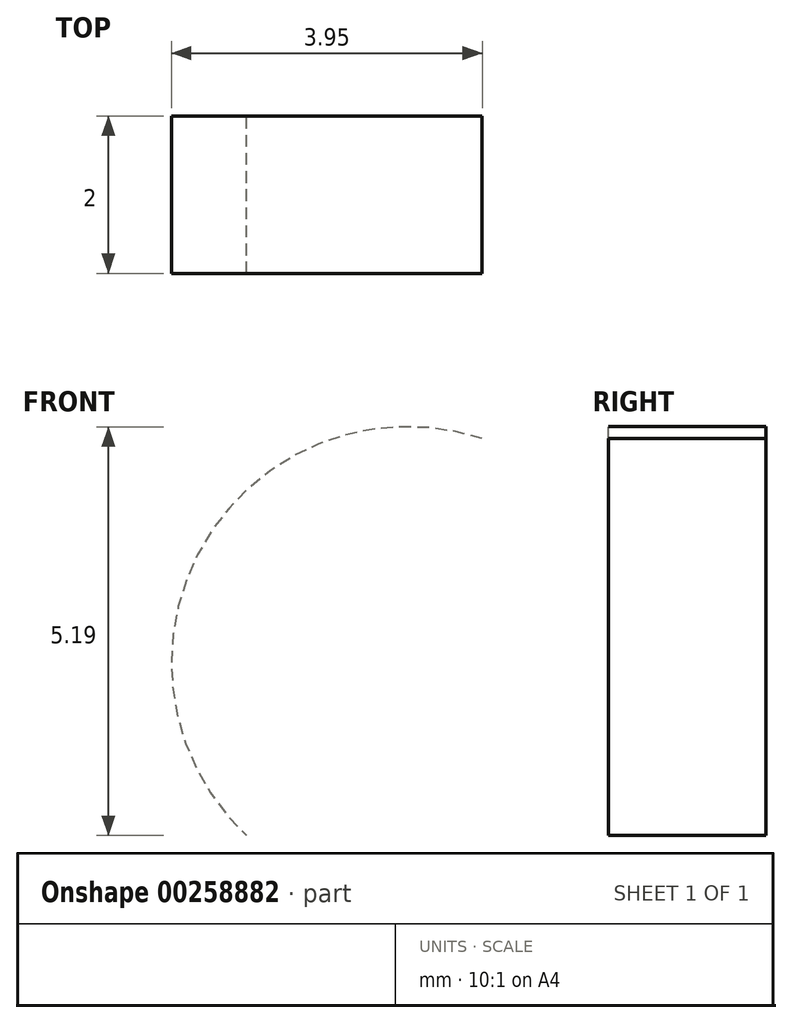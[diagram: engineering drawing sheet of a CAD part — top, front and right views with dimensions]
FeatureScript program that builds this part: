
annotation { "Feature Type Name" : "Feature", "Feature Type Description" : "" }
export const myFeature = defineFeature(function(context is Context, id is Id, definition is map)
    precondition{}
    {
        {
            var Q0;
            Q0=qCreatedBy(makeId("Front.planeOp"),FACE);
            var sketch = newSketch(context, id + "F0", { "sketchPlane" : qUnion([Q0])});
            skCircle(sketch, "E0", {"center": v(15, 2.03) * mm, "radius": 1.75 * mm});
            skCircle(sketch, "E1", {"center": v(0, -2.97) * mm, "radius": 1.75 * mm});
            skArc(sketch, "E2", {"start": v(17.04, -0.17) * mm, "mid": v(17.58, 3.56) * mm, "end": v(14.05, 4.88) * mm});
            skLineSegment(sketch, "E3", {"start": v(14.05, 4.88) * mm, "end": v(1.58, 0.72) * mm});
            skCircle(sketch, "E4.MirrorC", {"center": v(-15, 2.03) * mm, "radius": 1.75 * mm});
            skArc(sketch, "E5.MirrorC", {"start": v(-17.03, -0.17) * mm, "mid": v(-17.58, 3.56) * mm, "end": v(-14.05, 4.88) * mm});
            skLineSegment(sketch, "E6.MirrorCS", {"start": v(-14.05, 4.88) * mm, "end": v(-1.58, 0.72) * mm});
            skArc(sketch, "E7.filletArc", {"start": v(-1.58, 0.72) * mm, "mid": v(0, 0.47) * mm, "end": v(1.58, 0.72) * mm});
            skCircle(sketch, "E8", {"center": v(0, -9.47) * mm, "radius": 3.5 * mm});
            skArc(sketch, "E9", {"start": v(-3.23, -12.95) * mm, "mid": v(0, -14.22) * mm, "end": v(3.23, -12.95) * mm});
            skLineSegment(sketch, "E10", {"start": v(3.23, -12.95) * mm, "end": v(17.22, 0) * mm});
            skLineSegment(sketch, "E11.MirrorCS", {"start": v(-3.23, -12.95) * mm, "end": v(-17.22, 0) * mm});
            skSolve(sketch);
        }
        {
            var Q0;
            {var subQ0=sQuery(id+"F0.wireOp",EDGE,"E5.MirrorC");Q0=makeQuery(id+"F0.imprint","IMPRINT",FACE,{"disambiguationData":[TD([[makeQuery(id+"F0.imprint","IMPRINT",EDGE,{"derivedFrom":subQ0}),-1.0]])]});}
            extrude(context, id + "F1", {"entities" : qUnion([Q0]), "depth" : 2 * mm});
        }
    });
